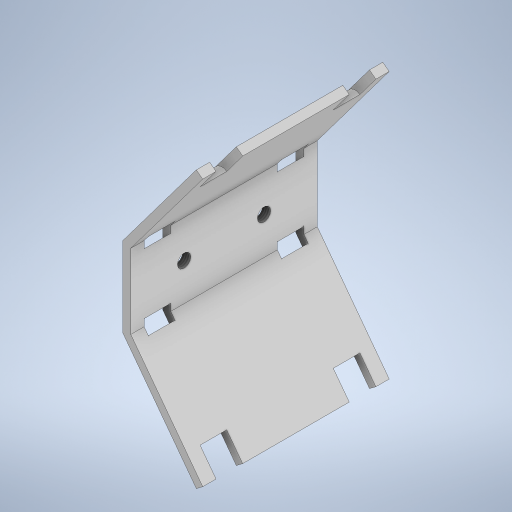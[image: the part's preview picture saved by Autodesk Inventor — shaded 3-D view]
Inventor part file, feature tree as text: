
AUTODESK INVENTOR PART (.ipt)
format: ipt  version: 2024 (Build 280153000, 153)  size: 363,008 bytes
history: native  units: in
note: dims shown in document units (in); Inventor stores cm internally (conversion verified against a paired STEP export)
features: sketch x5, extrude x4, plane x3, thread x2, shell x1, fillet x1, mirror x1, hole x1
ambient origin geometry x8: Origin, YZ Plane, XZ Plane, XY Plane, X Axis, Y Axis, Z Axis, Center Point
bodies: Body1 (feature_tree)
feature tree (18):
  extrude  "Extrusion2"  Depth=1.5748in
  shell  "Shell1"  Thickness=1.5748in
  extrude  "Extrusion3"  Depth=2.7559in TaperAngle=0.0deg
  extrude  "Extrusion4"  Depth=0.1181in
  fillet  "Fillet3"  Radius=0.1181in
  plane  "Work Plane1"
  plane  "Work Plane2"
  extrude  "Extrusion5"  Depth=0.3937in
  plane  "Work Plane3"
  mirror  "Mirror1"
  hole  "Hole2"  [1 undecoded]
  thread  "Thread8"  [1 undecoded]
  thread  "Thread9"  [1 undecoded]
  sketch  "Sketch2"  dims[d4=1.1811in d5=1.5748in d6=1.5748in]
  sketch  "Sketch4"  dims[d7=1.1811in d8=2.7559in d9=0.0in]
  sketch  "Sketch5"  dims[d10=0.1181in d11=0.1181in d12=0.1181in]
  sketch  "Sketch8"  dims[d13=0.1969in d54=0.3937in]
  sketch  "Sketch9"  dims[d55=0.3937in d56=0.1969in d57=0.1969in d58=0.3937in d59=0.3937in d60=0.0in d61=0.0in d62=0.1969in d63=0.1969in d64=0.3937in d65=0.3937in d66=0.3937in d67=0.0in d68=0.0in d69=0.1181in d87=0.3937in d88=0.1969in d89=0.1575in d90=0.1969in d91=0.3937in d92=0.1575in d93=0.0in d94=0.0in d95=1.1811in d96=1.1811in d97=0.1969in d98=0.2362in d99=0.1575in d100=0.0787in d101=90.0deg d102=0.1969in d103=0.0in d110=0.1181in d111=0.0in d112=0.1181in d113=0.0in d14=0.0344in d15=0.0197in d16=0.0344in]
note: 3 required parameter values undecoded (feature->parameter linkage not recoverable at this tier; creation-order binding heuristic only, values carry confidence <= 0.55)
